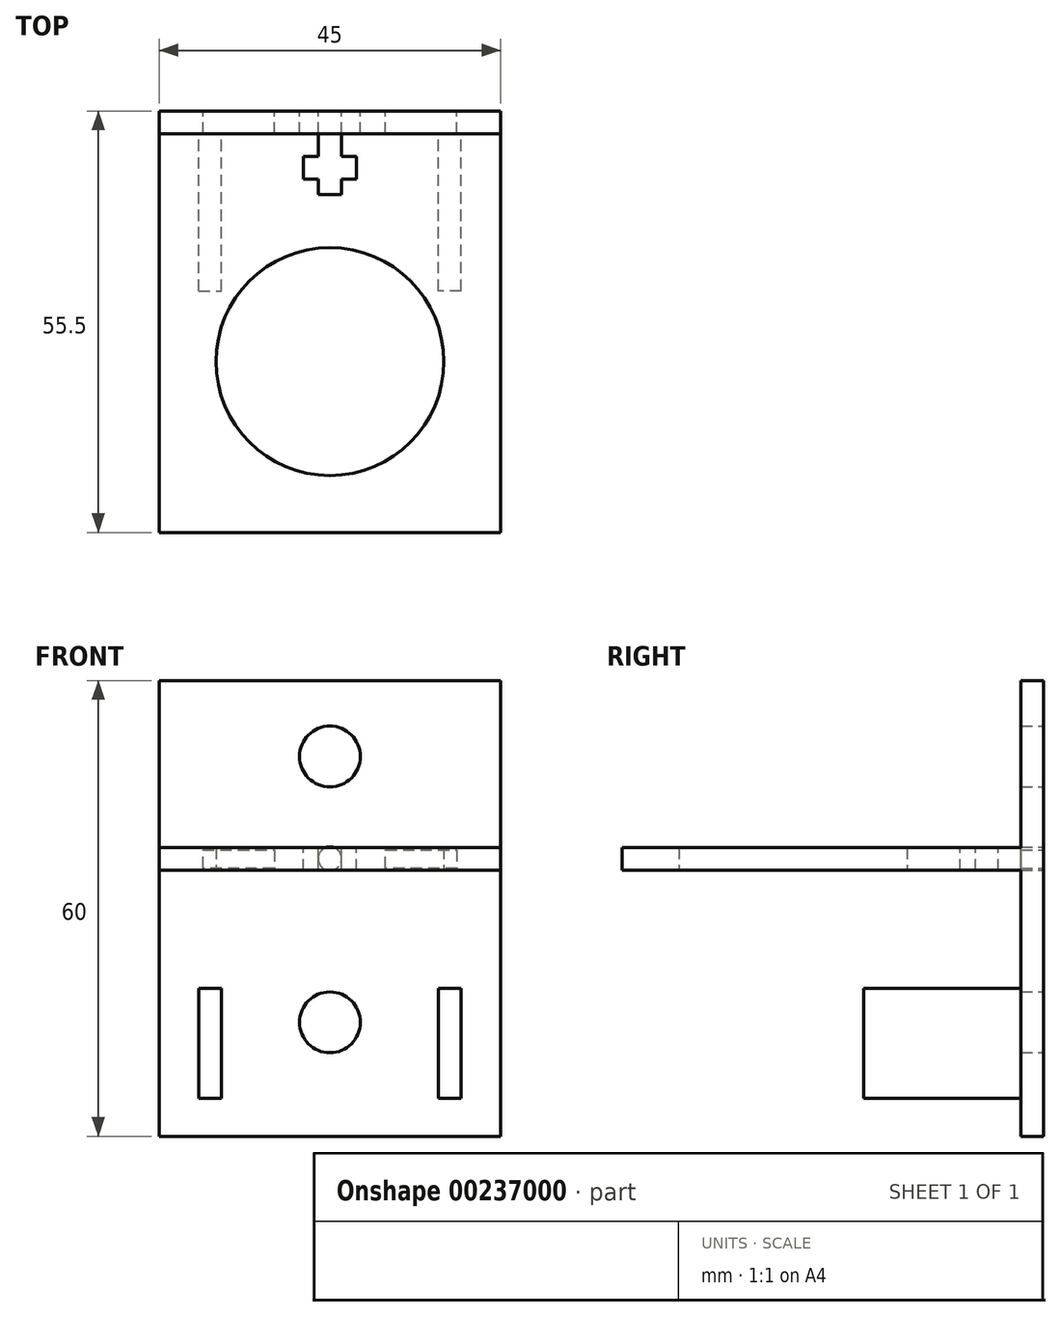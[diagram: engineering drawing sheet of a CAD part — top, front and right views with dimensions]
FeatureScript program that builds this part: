
annotation { "Feature Type Name" : "Feature", "Feature Type Description" : "" }
export const myFeature = defineFeature(function(context is Context, id is Id, definition is map)
    precondition{}
    {
        {
            var Q0;
            Q0=qCreatedBy(makeId("Top.planeOp"),FACE);
            var sketch = newSketch(context, id + "F0", { "sketchPlane" : qUnion([Q0])});
            skCircle(sketch, "E0", {"center": v(0, 0) * mm, "radius": 15 * mm});
            skLineSegment(sketch, "E1.bottom", {"start": v(-22.5, 30) * mm, "end": v(22.5, 30) * mm});
            skLineSegment(sketch, "E1.top", {"start": v(-22.5, -22.5) * mm, "end": v(22.5, -22.5) * mm});
            skLineSegment(sketch, "E1.left", {"start": v(-22.5, 30) * mm, "end": v(-22.5, -22.5) * mm});
            skLineSegment(sketch, "E1.right", {"start": v(22.5, 30) * mm, "end": v(22.5, -22.5) * mm});
            skLineSegment(sketch, "E2", {"start": v(0, 30) * mm, "end": v(0, -22.5) * mm, "construction": true});
            skSolve(sketch);
        }
        {
            var Q0;
            Q0=makeQuery(id+"F0.imprint","IMPRINT",FACE,{"disambiguationData":[TD([[makeQuery(id+"F0.imprint","IMPRINT",EDGE,{"derivedFrom":sQuery(id+"F0.wireOp",EDGE,"E0")}),-1.0]])]});
            extrude(context, id + "F1", {"entities" : qUnion([Q0]), "depth" : 3 * mm});
        }
        {
            var Q0;
            Q0=qCreatedBy(makeId("Front.planeOp"),FACE);
            cPlane(context, id + "F2", {"entities" : qUnion([Q0]), "cplaneType" : CPlaneType.OFFSET, "offset" : 30 * mm, "oppositeDirection" : true, "width" : 150 * mm, "height" : 150 * mm});
        }
        {
            var Q0;
            Q0=qCreatedBy(id+"F2.planeOp",FACE);
            var sketch = newSketch(context, id + "F3", { "sketchPlane" : qUnion([Q0])});
            skLineSegment(sketch, "E3.bottom", {"start": v(-22.5, 25) * mm, "end": v(22.5, 25) * mm});
            skLineSegment(sketch, "E3.top", {"start": v(-22.5, -35) * mm, "end": v(22.5, -35) * mm});
            skLineSegment(sketch, "E3.left", {"start": v(-22.5, 25) * mm, "end": v(-22.5, -35) * mm});
            skLineSegment(sketch, "E3.right", {"start": v(22.5, 25) * mm, "end": v(22.5, -35) * mm});
            skPoint(sketch, "E3.middle", {"position": v(0, -5) * mm});
            skSolve(sketch);
        }
        {
            var Q0;
            Q0=makeQuery(id+"F3.imprint","IMPRINT",FACE,{"disambiguationData":[TD([[makeQuery(id+"F3.imprint","IMPRINT",EDGE,{"derivedFrom":sQuery(id+"F3.wireOp",EDGE,"E3.bottom")}),-1.0]])]});
            extrude(context, id + "F4", {"entities" : qUnion([Q0]), "oppositeDirection" : true, "depth" : 3 * mm});
        }
        {
            var Q0;
            Q0=makeQuery(id+"F1.opExtrude","CAP_FACE",FACE,{"disambiguationData":[OSD([sQuery(id+"F0.wireOp",EDGE,"E0"),sQuery(id+"F0.wireOp",EDGE,"E1.bottom"),sQuery(id+"F0.wireOp",EDGE,"E1.top"),sQuery(id+"F0.wireOp",EDGE,"E1.left"),sQuery(id+"F0.wireOp",EDGE,"E1.right")])],"isStart":true});
            var sketch = newSketch(context, id + "F5", { "sketchPlane" : qUnion([Q0])});
            skCircle(sketch, "E4", {"center": v(0, 0) * mm, "radius": 20 * mm, "construction": true});
            skSolve(sketch);
        }
        {
            var Q0;
            Q0=makeQuery(id+"F1.opExtrude","CAP_FACE",FACE,{"disambiguationData":[OSD([sQuery(id+"F0.wireOp",EDGE,"E0"),sQuery(id+"F0.wireOp",EDGE,"E1.bottom"),sQuery(id+"F0.wireOp",EDGE,"E1.top"),sQuery(id+"F0.wireOp",EDGE,"E1.left"),sQuery(id+"F0.wireOp",EDGE,"E1.right")])],"isStart":false});
            var sketch = newSketch(context, id + "F6", { "sketchPlane" : qUnion([Q0])});
            skLineSegment(sketch, "E5.bottom", {"start": v(-1.55, 30) * mm, "end": v(1.55, 30) * mm});
            skLineSegment(sketch, "E5.top", {"start": v(-1.55, 22) * mm, "end": v(1.55, 22) * mm});
            skLineSegment(sketch, "E5.left", {"start": v(-1.55, 30) * mm, "end": v(-1.55, 27) * mm});
            skLineSegment(sketch, "E5.right", {"start": v(1.55, 30) * mm, "end": v(1.55, 27) * mm});
            skLineSegment(sketch, "E6.bottom", {"start": v(-3.5, 27) * mm, "end": v(-1.55, 27) * mm});
            skLineSegment(sketch, "E6.top", {"start": v(-3.5, 24) * mm, "end": v(0, 24) * mm});
            skLineSegment(sketch, "E6.left", {"start": v(-3.5, 27) * mm, "end": v(-3.5, 24) * mm});
            skLineSegment(sketch, "E6.right", {"start": v(3.5, 27) * mm, "end": v(3.5, 24) * mm});
            skPoint(sketch, "E7", {"position": v(0, 24) * mm});
            skLineSegment(sketch, "E8.trimOffspring", {"start": v(-1.55, 24) * mm, "end": v(-1.55, 22) * mm});
            skLineSegment(sketch, "E9.trimOffspring", {"start": v(1.55, 27) * mm, "end": v(3.5, 27) * mm});
            skLineSegment(sketch, "E10.trimOffspring", {"start": v(1.55, 24) * mm, "end": v(1.55, 22) * mm});
            skLineSegment(sketch, "E11.trimOffspring", {"start": v(1.55, 24) * mm, "end": v(3.5, 24) * mm});
            skSolve(sketch);
        }
        {
            var Q0;
            Q0=makeQuery(id+"F6.imprint","IMPRINT",FACE,{"disambiguationData":[TD([[makeQuery(id+"F6.imprint","IMPRINT",EDGE,{"derivedFrom":sQuery(id+"F6.wireOp",EDGE,"E5.bottom")}),-1.0]])]});
            extrude(context, id + "F7", {"entities" : qUnion([Q0]), "operationType" : NewBodyOperationType.REMOVE, "endBound" : BoundingType.THROUGH_ALL, "oppositeDirection" : true, "depth" : 25 * mm});
        }
        {
            var Q0;
            Q0=makeQuery(id+"F4.opExtrude","CAP_FACE",FACE,{"disambiguationData":[OSD([sQuery(id+"F3.wireOp",EDGE,"E3.bottom"),sQuery(id+"F3.wireOp",EDGE,"E3.top"),sQuery(id+"F3.wireOp",EDGE,"E3.left"),sQuery(id+"F3.wireOp",EDGE,"E3.right")])],"isStart":false});
            var sketch = newSketch(context, id + "F8", { "sketchPlane" : qUnion([Q0])});
            skCircle(sketch, "E12", {"center": v(0, 1.55) * mm, "radius": 1.55 * mm});
            skSolve(sketch);
        }
        {
            var Q0;
            Q0=makeQuery(id+"F8.imprint","IMPRINT",FACE,{"disambiguationData":[TD([[makeQuery(id+"F8.imprint","IMPRINT",EDGE,{"derivedFrom":sQuery(id+"F8.wireOp",EDGE,"E12")}),1.0]])]});
            extrude(context, id + "F9", {"entities" : qUnion([Q0]), "operationType" : NewBodyOperationType.REMOVE, "oppositeDirection" : true, "depth" : 3 * mm});
        }
        {
            var Q0;
            {var subQ0=sQuery(id+"F0.wireOp",EDGE,"E1.right");var subQ3=sQuery(id+"F0.wireOp",EDGE,"E1.bottom");Q0=makeQuery(id+"F7.boolean.opBoolean","SPLIT",FACE,{"disambiguationData":[TD([makeQuery(id+"F1.opExtrude","SWEPT_FACE",FACE,{"disambiguationData":[OSD([subQ0])]})])],"derivedFrom":makeQuery(id+"F1.opExtrude","SWEPT_FACE",FACE,{"disambiguationData":[OSD([subQ3])]})});}
            var sketch = newSketch(context, id + "F10", { "sketchPlane" : qUnion([Q0])});
            skLineSegment(sketch, "E13.bottom", {"start": v(-17.02, 3) * mm, "end": v(-7.02, 3) * mm});
            skLineSegment(sketch, "E13.top", {"start": v(-17.02, 0) * mm, "end": v(-7.02, 0) * mm});
            skLineSegment(sketch, "E13.left", {"start": v(-17.02, 3) * mm, "end": v(-17.02, 0) * mm});
            skLineSegment(sketch, "E13.right", {"start": v(-7.02, 3) * mm, "end": v(-7.02, 0) * mm});
            skLineSegment(sketch, "E14.bottom", {"start": v(7.02, 3) * mm, "end": v(17.02, 3) * mm});
            skLineSegment(sketch, "E14.top", {"start": v(7.02, 0) * mm, "end": v(17.02, 0) * mm});
            skLineSegment(sketch, "E14.left", {"start": v(7.02, 3) * mm, "end": v(7.02, 0) * mm});
            skLineSegment(sketch, "E14.right", {"start": v(17.02, 3) * mm, "end": v(17.02, 0) * mm});
            skSolve(sketch);
        }
        {
            var Q0;
            Q0=makeQuery(id+"F10.imprint","IMPRINT",FACE,{"disambiguationData":[TD([[makeQuery(id+"F10.imprint","IMPRINT",EDGE,{"derivedFrom":sQuery(id+"F10.wireOp",EDGE,"E13.bottom")}),1.0]])]});
            var Q1;
            Q1=makeQuery(id+"F10.imprint","IMPRINT",FACE,{"disambiguationData":[TD([[makeQuery(id+"F10.imprint","IMPRINT",EDGE,{"derivedFrom":sQuery(id+"F10.wireOp",EDGE,"E14.bottom")}),-1.0]])]});
            extrude(context, id + "F11", {"entities" : qUnion([Q0, Q1]), "operationType" : NewBodyOperationType.ADD, "depth" : 3 * mm});
        }
        {
            var Q0;
            Q0=makeQuery(id+"F4.opExtrude","CAP_FACE",FACE,{"disambiguationData":[OSD([sQuery(id+"F3.wireOp",EDGE,"E3.bottom"),sQuery(id+"F3.wireOp",EDGE,"E3.top"),sQuery(id+"F3.wireOp",EDGE,"E3.left"),sQuery(id+"F3.wireOp",EDGE,"E3.right")])],"isStart":false});
            var sketch = newSketch(context, id + "F12", { "sketchPlane" : qUnion([Q0])});
            skLineSegment(sketch, "E15.0", {"start": v(-7.32, 0.3) * mm, "end": v(-7.32, 2.7) * mm});
            skLineSegment(sketch, "E15.1", {"start": v(-16.72, 0.3) * mm, "end": v(-7.32, 0.3) * mm});
            skLineSegment(sketch, "E15.2", {"start": v(-16.72, 2.7) * mm, "end": v(-16.72, 0.3) * mm});
            skLineSegment(sketch, "E15.3", {"start": v(-7.32, 2.7) * mm, "end": v(-16.72, 2.7) * mm});
            skLineSegment(sketch, "E16.0", {"start": v(7.32, 2.7) * mm, "end": v(7.32, 0.3) * mm});
            skLineSegment(sketch, "E16.1", {"start": v(16.72, 2.7) * mm, "end": v(7.32, 2.7) * mm});
            skLineSegment(sketch, "E16.2", {"start": v(16.72, 0.3) * mm, "end": v(16.72, 2.7) * mm});
            skLineSegment(sketch, "E16.3", {"start": v(7.32, 0.3) * mm, "end": v(16.72, 0.3) * mm});
            skSolve(sketch);
        }
        {
            var Q0;
            Q0 = qSketchRegion(id + "F12", true);
            extrude(context, id + "F13", {"entities" : qUnion([Q0]), "operationType" : NewBodyOperationType.REMOVE, "oppositeDirection" : true, "depth" : 3 * mm});
        }
        {
            var Q0;
            Q0=makeQuery(id+"F4.opExtrude","CAP_FACE",FACE,{"disambiguationData":[OSD([sQuery(id+"F3.wireOp",EDGE,"E3.bottom"),sQuery(id+"F3.wireOp",EDGE,"E3.top"),sQuery(id+"F3.wireOp",EDGE,"E3.left"),sQuery(id+"F3.wireOp",EDGE,"E3.right")])],"isStart":false});
            var sketch = newSketch(context, id + "F14", { "sketchPlane" : qUnion([Q0])});
            skCircle(sketch, "E17", {"center": v(0, 15) * mm, "radius": 4 * mm});
            skCircle(sketch, "E18", {"center": v(0, -20) * mm, "radius": 4 * mm});
            skSolve(sketch);
        }
        {
            var Q0;
            Q0=makeQuery(id+"F14.imprint","IMPRINT",FACE,{"disambiguationData":[TD([[makeQuery(id+"F14.imprint","IMPRINT",EDGE,{"derivedFrom":sQuery(id+"F14.wireOp",EDGE,"E17")}),1.0]])]});
            var Q1;
            Q1=makeQuery(id+"F14.imprint","IMPRINT",FACE,{"disambiguationData":[TD([[makeQuery(id+"F14.imprint","IMPRINT",EDGE,{"derivedFrom":sQuery(id+"F14.wireOp",EDGE,"E18")}),1.0]])]});
            extrude(context, id + "F15", {"entities" : qUnion([Q0, Q1]), "operationType" : NewBodyOperationType.REMOVE, "oppositeDirection" : true, "depth" : 3 * mm});
        }
        {
            var Q0;
            Q0=qCreatedBy(id+"F2.planeOp",FACE);
            var sketch = newSketch(context, id + "F16", { "sketchPlane" : qUnion([Q0])});
            skLineSegment(sketch, "E19", {"start": v(0, 25) * mm, "end": v(0, -35) * mm, "construction": true});
            skLineSegment(sketch, "E20.bottom", {"start": v(-17.3, -15.5) * mm, "end": v(-14.3, -15.5) * mm});
            skLineSegment(sketch, "E20.top", {"start": v(-17.3, -30) * mm, "end": v(-14.3, -30) * mm});
            skLineSegment(sketch, "E20.left", {"start": v(-17.3, -15.5) * mm, "end": v(-17.3, -30) * mm});
            skLineSegment(sketch, "E20.right", {"start": v(-14.3, -15.5) * mm, "end": v(-14.3, -30) * mm});
            skLineSegment(sketch, "E21.MirrorCS", {"start": v(14.3, -15.5) * mm, "end": v(14.3, -30) * mm});
            skLineSegment(sketch, "E22.MirrorCS", {"start": v(17.3, -15.5) * mm, "end": v(14.3, -15.5) * mm});
            skLineSegment(sketch, "E23.MirrorCS", {"start": v(17.3, -15.5) * mm, "end": v(17.3, -30) * mm});
            skLineSegment(sketch, "E24.MirrorCS", {"start": v(17.3, -30) * mm, "end": v(14.3, -30) * mm});
            skSolve(sketch);
        }
        {
            var Q0;
            Q0=makeQuery(id+"F16.imprint","IMPRINT",FACE,{"disambiguationData":[TD([[makeQuery(id+"F16.imprint","IMPRINT",EDGE,{"derivedFrom":sQuery(id+"F16.wireOp",EDGE,"E20.bottom")}),-1.0]])]});
            var Q1;
            Q1=makeQuery(id+"F16.imprint","IMPRINT",FACE,{"disambiguationData":[TD([[makeQuery(id+"F16.imprint","IMPRINT",EDGE,{"derivedFrom":sQuery(id+"F16.wireOp",EDGE,"E21.MirrorCS")}),1.0]])]});
            extrude(context, id + "F17", {"entities" : qUnion([Q0, Q1]), "depth" : 20.7 * mm});
        }
    });
